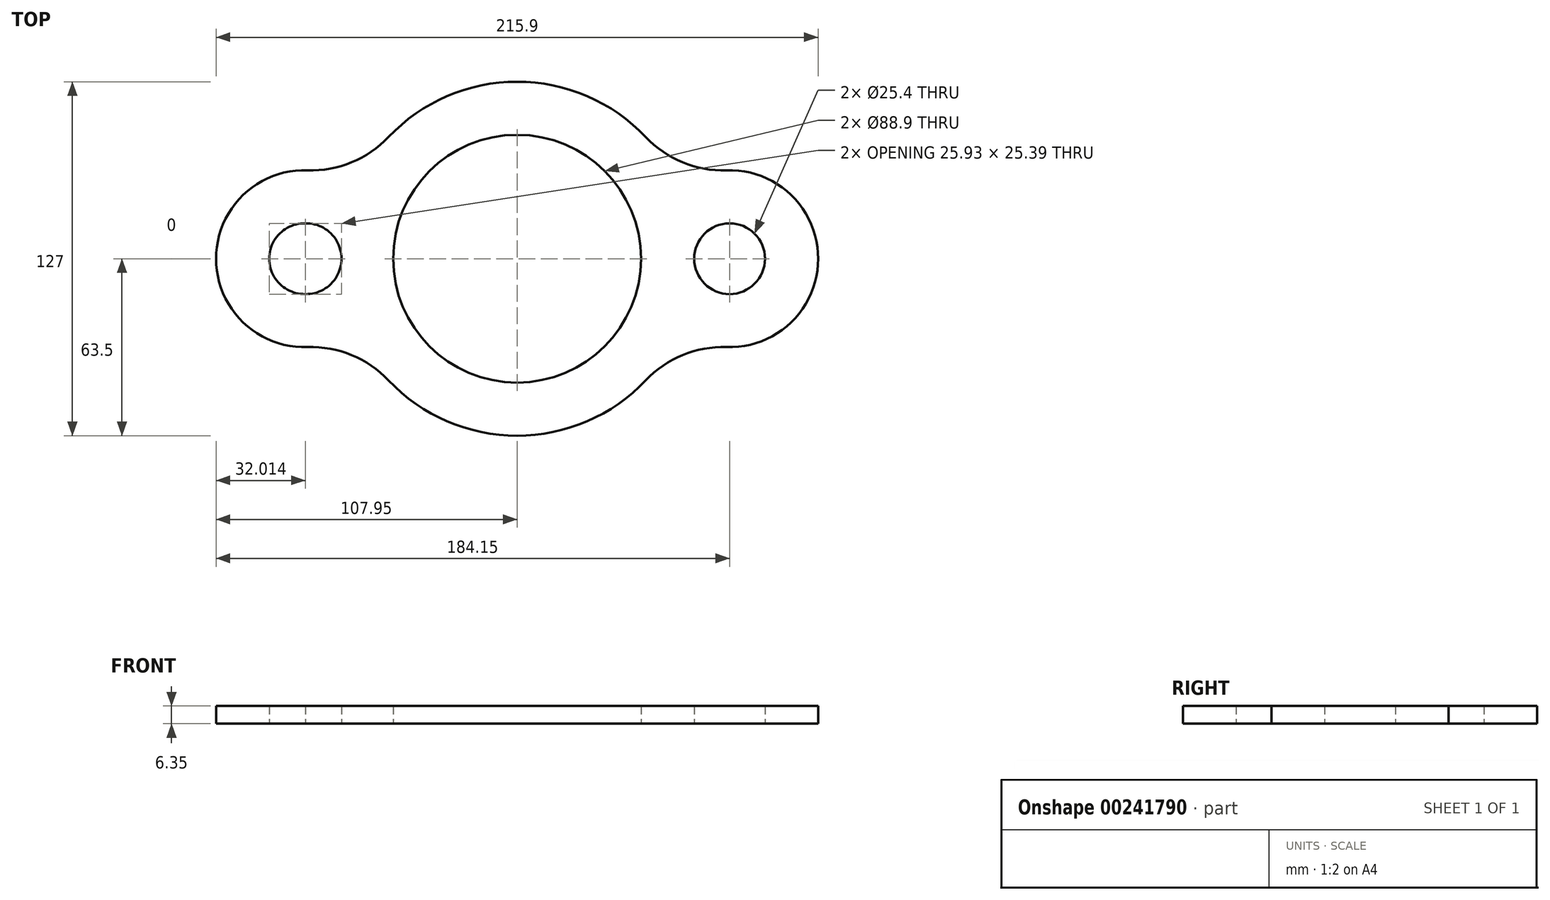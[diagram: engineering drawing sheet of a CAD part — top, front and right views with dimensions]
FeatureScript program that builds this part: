
annotation { "Feature Type Name" : "Feature", "Feature Type Description" : "" }
export const myFeature = defineFeature(function(context is Context, id is Id, definition is map)
    precondition{}
    {
        {
            var Q0;
            Q0=qCreatedBy(makeId("Top.planeOp"),FACE);
            var sketch = newSketch(context, id + "F0", { "sketchPlane" : qUnion([Q0])});
            skCircle(sketch, "E0", {"center": v(0, 0) * mm, "radius": 44.45 * mm});
            skLineSegment(sketch, "E1", {"start": v(0, 0) * mm, "end": v(-75.67, 0) * mm, "construction": true});
            skCircle(sketch, "E2", {"center": v(-75.67, 0) * mm, "radius": 12.7 * mm});
            skLineSegment(sketch, "E3", {"start": v(0, 0) * mm, "end": v(76.2, 0) * mm, "construction": true});
            skCircle(sketch, "E4", {"center": v(76.2, 0) * mm, "radius": 12.7 * mm});
            skArc(sketch, "E5", {"start": v(75.12, -31.73) * mm, "mid": v(107.95, 0) * mm, "end": v(75.12, 31.73) * mm});
            skArc(sketch, "E6.MirrorC", {"start": v(-75.12, -31.73) * mm, "mid": v(-107.95, 0) * mm, "end": v(-75.12, 31.73) * mm});
            skArc(sketch, "E7.trimOffspring", {"start": v(-46.14, -43.63) * mm, "mid": v(0, -63.5) * mm, "end": v(46.14, -43.63) * mm});
            skArc(sketch, "E8.trimOffspring", {"start": v(46.14, 43.63) * mm, "mid": v(0, 63.5) * mm, "end": v(-46.14, 43.63) * mm});
            skPoint(sketch, "E9.visualSharp", {"position": v(-57.94, 25.98) * mm});
            skArc(sketch, "E9.filletArc", {"start": v(-75.12, 31.73) * mm, "mid": v(-59.35, 34.56) * mm, "end": v(-46.14, 43.63) * mm});
            skPoint(sketch, "E10.visualSharp", {"position": v(-57.94, -25.98) * mm});
            skArc(sketch, "E10.filletArc", {"start": v(-46.14, -43.63) * mm, "mid": v(-59.35, -34.56) * mm, "end": v(-75.12, -31.73) * mm});
            skPoint(sketch, "E11.visualSharp", {"position": v(57.94, -25.98) * mm});
            skArc(sketch, "E11.filletArc", {"start": v(75.12, -31.73) * mm, "mid": v(59.35, -34.56) * mm, "end": v(46.14, -43.63) * mm});
            skPoint(sketch, "E12.visualSharp", {"position": v(57.94, 25.98) * mm});
            skArc(sketch, "E12.filletArc", {"start": v(46.14, 43.63) * mm, "mid": v(59.35, 34.56) * mm, "end": v(75.12, 31.73) * mm});
            skArc(sketch, "E13.MirrorCS", {"start": v(-46.14, 43.63) * mm, "mid": v(-59.35, 34.56) * mm, "end": v(-75.12, 31.73) * mm});
            skCircle(sketch, "E14.MirrorC", {"center": v(-76.2, 0) * mm, "radius": 12.7 * mm});
            skLineSegment(sketch, "E15.MirrorCS", {"start": v(0, 0) * mm, "end": v(-76.2, 0) * mm, "construction": true});
            skArc(sketch, "E16.MirrorCS", {"start": v(-75.12, -31.73) * mm, "mid": v(-59.35, -34.56) * mm, "end": v(-46.14, -43.63) * mm});
            skArc(sketch, "E17.MirrorCS", {"start": v(46.14, -43.63) * mm, "mid": v(0, -63.5) * mm, "end": v(-46.14, -43.63) * mm});
            skArc(sketch, "E18.MirrorCS", {"start": v(-46.14, 43.63) * mm, "mid": v(0, 63.5) * mm, "end": v(46.14, 43.63) * mm});
            skSolve(sketch);
        }
        {
            var Q0;
            Q0=makeQuery(id+"F0.imprint","IMPRINT",FACE,{"disambiguationData":[TD([[makeQuery(id+"F0.imprint","IMPRINT",EDGE,{"derivedFrom":sQuery(id+"F0.wireOp",EDGE,"E0")}),-1.0]])]});
            extrude(context, id + "F1", {"entities" : qUnion([Q0]), "depth" : 6.35 * mm});
        }
        {
            var Q0;
            Q0=makeQuery(id+"F0.imprint","IMPRINT",FACE,{"disambiguationData":[TD([[makeQuery(id+"F0.imprint","IMPRINT",EDGE,{"derivedFrom":sQuery(id+"F0.wireOp",EDGE,"E4")}),-1.0]])]});
            extrude(context, id + "F2", {"entities" : qUnion([Q0]), "depth" : 6.35 * mm});
        }
    });
